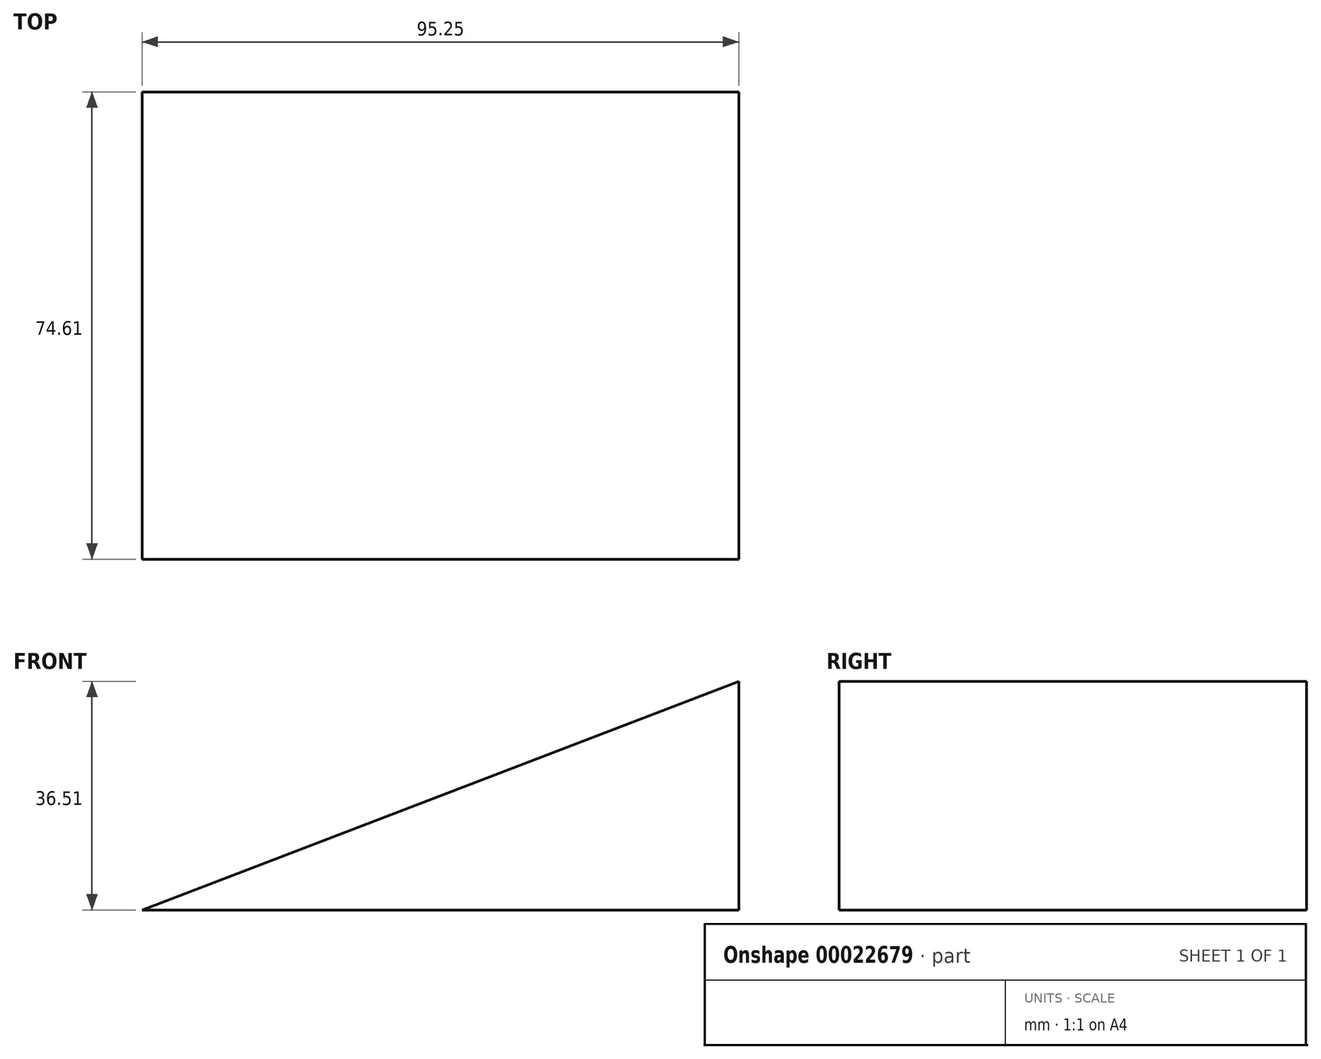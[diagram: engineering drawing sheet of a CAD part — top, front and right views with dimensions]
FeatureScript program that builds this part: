
annotation { "Feature Type Name" : "Feature", "Feature Type Description" : "" }
export const myFeature = defineFeature(function(context is Context, id is Id, definition is map)
    precondition{}
    {
        {
            var Q0;
            Q0=qCreatedBy(makeId("Front.planeOp"),FACE);
            var sketch = newSketch(context, id + "F0", { "sketchPlane" : qUnion([Q0])});
            skLineSegment(sketch, "E0", {"start": v(0, 0) * mm, "end": v(95.25, 0) * mm});
            skLineSegment(sketch, "E1", {"start": v(95.25, 0) * mm, "end": v(95.25, 36.51) * mm});
            skLineSegment(sketch, "E2", {"start": v(95.25, 36.51) * mm, "end": v(0, 0) * mm});
            skSolve(sketch);
        }
        {
            var Q0;
            Q0=makeQuery(id+"F0.imprint","IMPRINT",FACE,{"disambiguationData":[TD([[makeQuery(id+"F0.imprint","IMPRINT",EDGE,{"derivedFrom":sQuery(id+"F0.wireOp",EDGE,"E0")}),1.0]])]});
            extrude(context, id + "F1", {"entities" : qUnion([Q0]), "depth" : 38.1 * mm});
        }
        {
            var Q0;
            Q0=qSketchRegion(id+"F0",true);
            var Q1;
            Q1=makeQuery(id+"F1.opExtrude","CAP_FACE",FACE,{"disambiguationData":[OSD([sQuery(id+"F0.wireOp",EDGE,"E0"),sQuery(id+"F0.wireOp",EDGE,"E1"),sQuery(id+"F0.wireOp",EDGE,"E2")])],"isStart":false});
            extrude(context, id + "F2", {"entities" : qUnion([Q0, Q1]), "operationType" : NewBodyOperationType.ADD, "depth" : 36.5 * mm});
        }
    });
